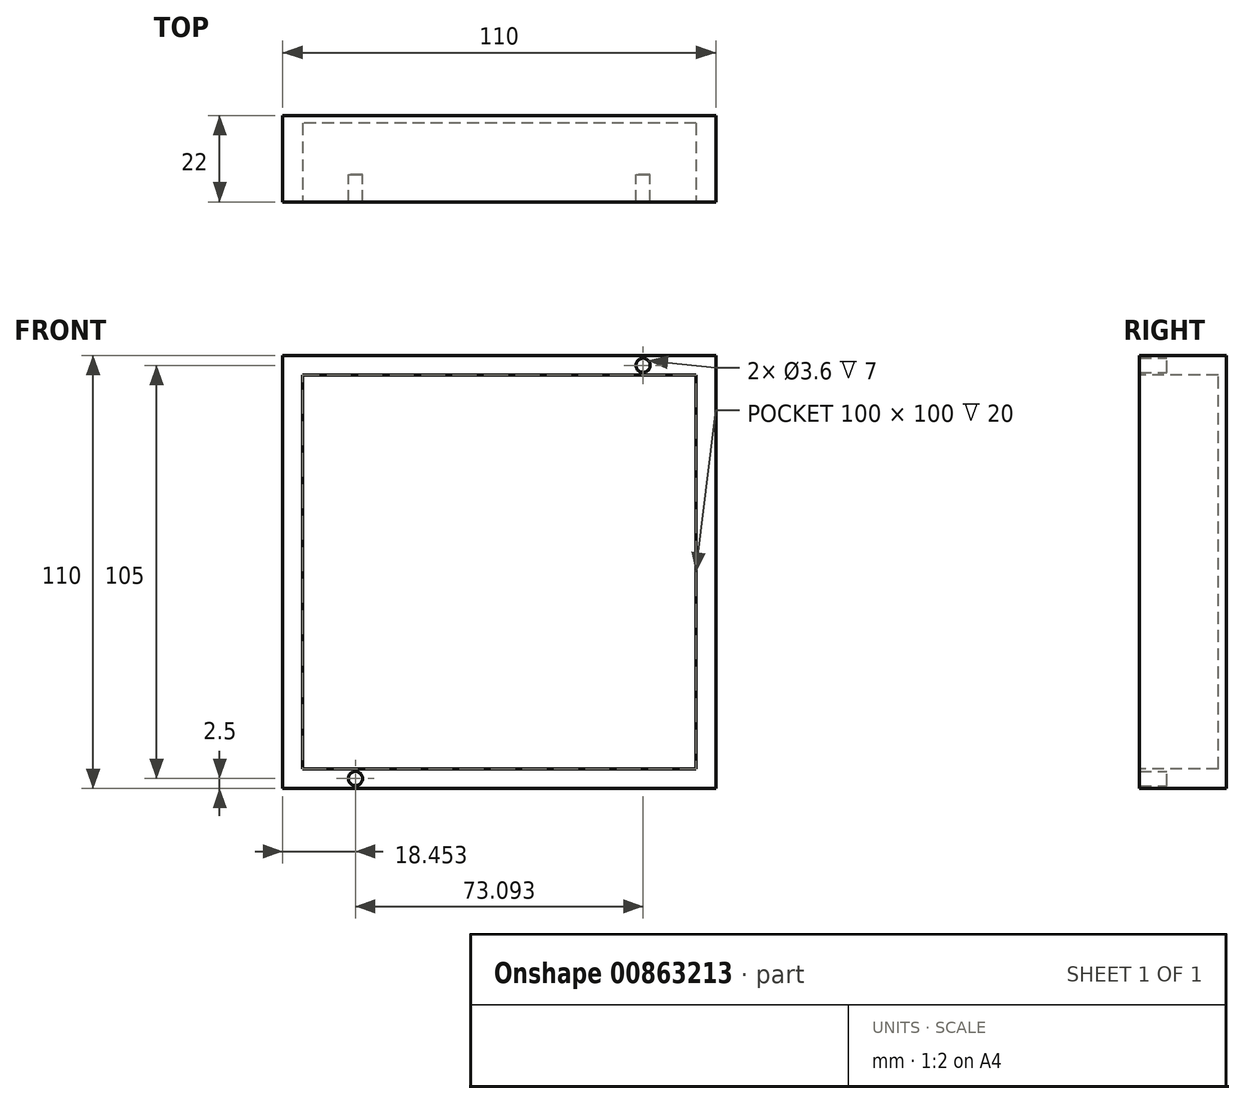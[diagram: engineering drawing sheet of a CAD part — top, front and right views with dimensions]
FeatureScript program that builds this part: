
annotation { "Feature Type Name" : "Feature", "Feature Type Description" : "" }
export const myFeature = defineFeature(function(context is Context, id is Id, definition is map)
    precondition{}
    {
        {
            var Q0;
            Q0=qCreatedBy(makeId("Front.planeOp"),FACE);
            var sketch = newSketch(context, id + "F0", { "sketchPlane" : qUnion([Q0])});
            skLineSegment(sketch, "E0.bottom", {"start": v(55, -55) * mm, "end": v(-55, -55) * mm});
            skLineSegment(sketch, "E0.top", {"start": v(55, 55) * mm, "end": v(-55, 55) * mm});
            skLineSegment(sketch, "E0.left", {"start": v(55, -55) * mm, "end": v(55, 55) * mm});
            skLineSegment(sketch, "E0.right", {"start": v(-55, -55) * mm, "end": v(-55, 55) * mm});
            skPoint(sketch, "E0.middle", {"position": v(0, 0) * mm});
            skSolve(sketch);
        }
        {
            var Q0;
            Q0=makeQuery(id+"F0.imprint","IMPRINT",FACE,{"disambiguationData":[TD([[makeQuery(id+"F0.imprint","IMPRINT",EDGE,{"derivedFrom":sQuery(id+"F0.wireOp",EDGE,"E0.bottom")}),-1.0]])]});
            extrude(context, id + "F1", {"entities" : qUnion([Q0]), "depth" : 15 * mm, "offsetDistance" : 25 * mm});
        }
        {
            var Q0;
            Q0=makeQuery(id+"F1.opExtrude","CAP_FACE",FACE,{"disambiguationData":[OSD([sQuery(id+"F0.wireOp",EDGE,"E0.bottom"),sQuery(id+"F0.wireOp",EDGE,"E0.top"),sQuery(id+"F0.wireOp",EDGE,"E0.left"),sQuery(id+"F0.wireOp",EDGE,"E0.right")])],"isStart":false});
            var sketch = newSketch(context, id + "F2", { "sketchPlane" : qUnion([Q0])});
            skLineSegment(sketch, "E1.bottom", {"start": v(50, -50) * mm, "end": v(-50, -50) * mm});
            skLineSegment(sketch, "E1.top", {"start": v(50, 50) * mm, "end": v(-50, 50) * mm});
            skLineSegment(sketch, "E1.left", {"start": v(50, -50) * mm, "end": v(50, 50) * mm});
            skLineSegment(sketch, "E1.right", {"start": v(-50, -50) * mm, "end": v(-50, 50) * mm});
            skPoint(sketch, "E1.middle", {"position": v(0, 0) * mm});
            skSolve(sketch);
        }
        {
            var Q0;
            Q0=makeQuery(id+"F2.imprint","IMPRINT",FACE,{"disambiguationData":[TD([[makeQuery(id+"F2.imprint","IMPRINT",EDGE,{"derivedFrom":sQuery(id+"F2.wireOp",EDGE,"E1.bottom")}),-1.0]])]});
            extrude(context, id + "F3", {"entities" : qUnion([Q0]), "operationType" : NewBodyOperationType.REMOVE, "oppositeDirection" : true, "depth" : 13 * mm, "offsetDistance" : 25 * mm});
        }
        {
            var Q0;
            Q0=makeQuery(id+"F1.opExtrude","CAP_FACE",FACE,{"disambiguationData":[OSD([sQuery(id+"F0.wireOp",EDGE,"E0.bottom"),sQuery(id+"F0.wireOp",EDGE,"E0.top"),sQuery(id+"F0.wireOp",EDGE,"E0.left"),sQuery(id+"F0.wireOp",EDGE,"E0.right")])],"isStart":false});
            var sketch = newSketch(context, id + "F4", { "sketchPlane" : qUnion([Q0])});
            skCircle(sketch, "E2", {"center": v(-36.55, 52.5) * mm, "radius": 1.8 * mm});
            skCircle(sketch, "E3.MirrorC", {"center": v(36.55, 52.5) * mm, "radius": 1.8 * mm});
            skCircle(sketch, "E4.MirrorC", {"center": v(36.55, -52.5) * mm, "radius": 1.8 * mm});
            skCircle(sketch, "E5.MirrorC", {"center": v(-36.55, -52.5) * mm, "radius": 1.8 * mm});
            skSolve(sketch);
        }
        {
            var Q0;
            Q0=makeQuery(id+"F4.imprint","IMPRINT",FACE,{"disambiguationData":[TD([[makeQuery(id+"F4.imprint","IMPRINT",EDGE,{"derivedFrom":sQuery(id+"F4.wireOp",EDGE,"E2")}),1.0]])]});
            var Q1;
            Q1=makeQuery(id+"F4.imprint","IMPRINT",FACE,{"disambiguationData":[TD([[makeQuery(id+"F4.imprint","IMPRINT",EDGE,{"derivedFrom":sQuery(id+"F4.wireOp",EDGE,"E3.MirrorC")}),-1.0]])]});
            var Q2;
            Q2=makeQuery(id+"F4.imprint","IMPRINT",FACE,{"disambiguationData":[TD([[makeQuery(id+"F4.imprint","IMPRINT",EDGE,{"derivedFrom":sQuery(id+"F4.wireOp",EDGE,"E5.MirrorC")}),-1.0]])]});
            var Q3;
            Q3=makeQuery(id+"F4.imprint","IMPRINT",FACE,{"disambiguationData":[TD([[makeQuery(id+"F4.imprint","IMPRINT",EDGE,{"derivedFrom":sQuery(id+"F4.wireOp",EDGE,"E4.MirrorC")}),1.0]])]});
            extrude(context, id + "F5", {"entities" : qUnion([Q0, Q1, Q2, Q3]), "operationType" : NewBodyOperationType.ADD, "depth" : 7 * mm, "offsetDistance" : 25 * mm});
        }
    });
